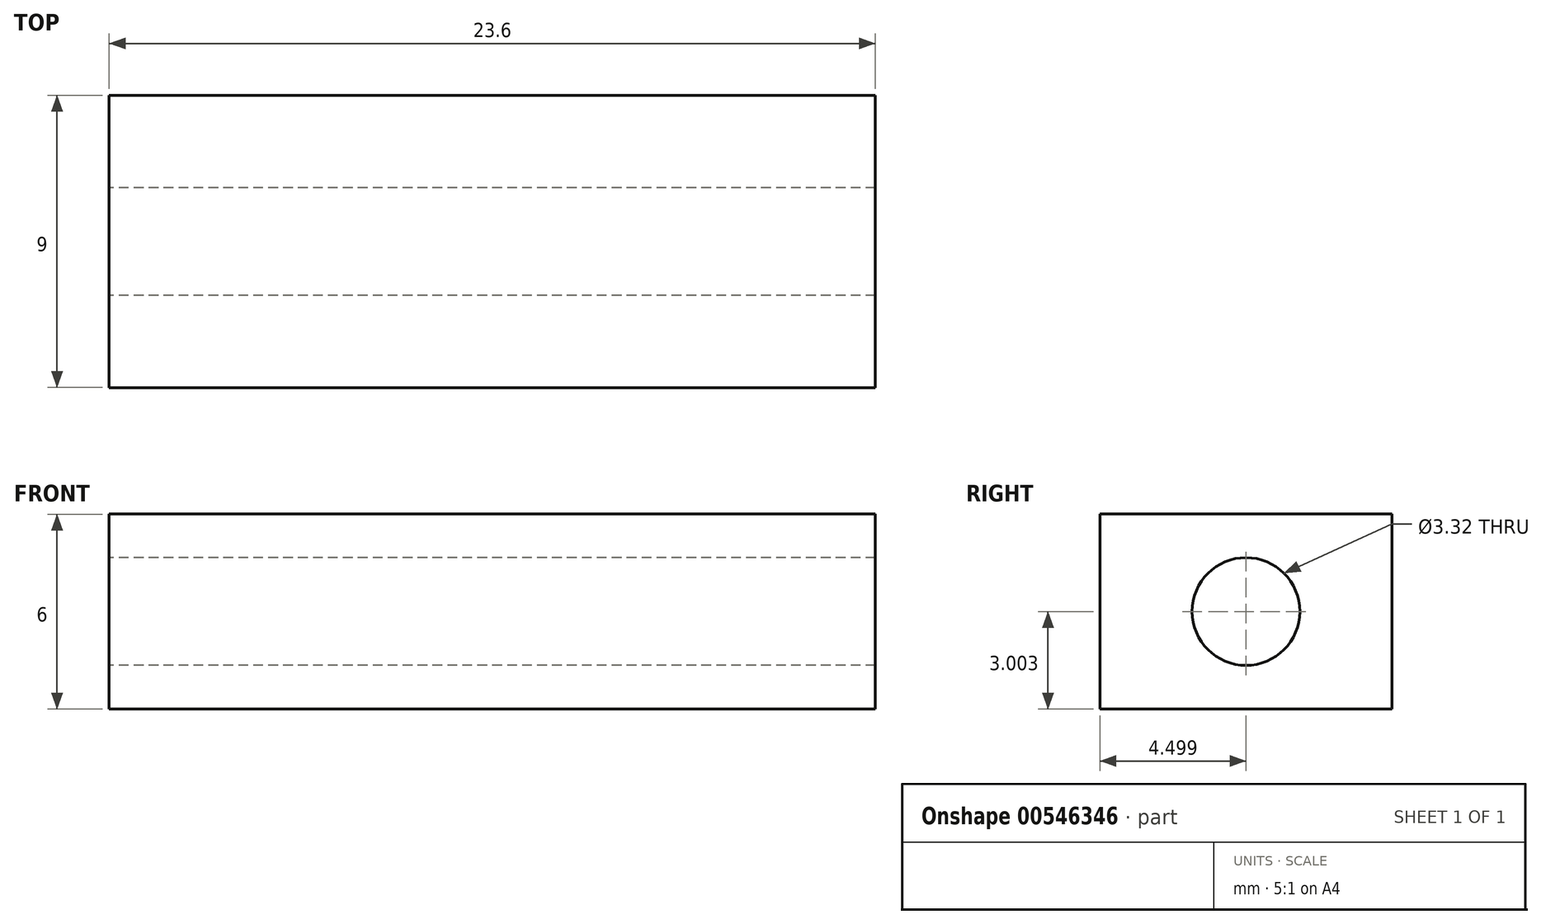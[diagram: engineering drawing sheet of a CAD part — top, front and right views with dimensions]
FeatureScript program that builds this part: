
annotation { "Feature Type Name" : "Feature", "Feature Type Description" : "" }
export const myFeature = defineFeature(function(context is Context, id is Id, definition is map)
    precondition{}
    {
        {
            var Q0;
            Q0=qCreatedBy(makeId("Right.planeOp"),FACE);
            var sketch = newSketch(context, id + "F0", { "sketchPlane" : qUnion([Q0])});
            skLineSegment(sketch, "E0.bottom", {"start": v(3.14, 4.48) * mm, "end": v(12.14, 4.48) * mm});
            skLineSegment(sketch, "E0.top", {"start": v(3.14, -1.52) * mm, "end": v(12.14, -1.52) * mm});
            skLineSegment(sketch, "E0.left", {"start": v(3.14, 4.48) * mm, "end": v(3.14, -1.52) * mm});
            skLineSegment(sketch, "E0.right", {"start": v(12.14, 4.48) * mm, "end": v(12.14, -1.52) * mm});
            skCircle(sketch, "E1", {"center": v(7.64, 1.48) * mm, "radius": 1.66 * mm});
            skSolve(sketch);
        }
        {
            var Q0;
            Q0=makeQuery(id+"F0.imprint","IMPRINT",FACE,{"disambiguationData":[TD([[makeQuery(id+"F0.imprint","IMPRINT",EDGE,{"derivedFrom":sQuery(id+"F0.wireOp",EDGE,"E0.bottom")}),-1.0]])]});
            extrude(context, id + "F1", {"entities" : qUnion([Q0]), "depth" : 23.6 * mm, "offsetDistance" : 25 * mm});
        }
    });
